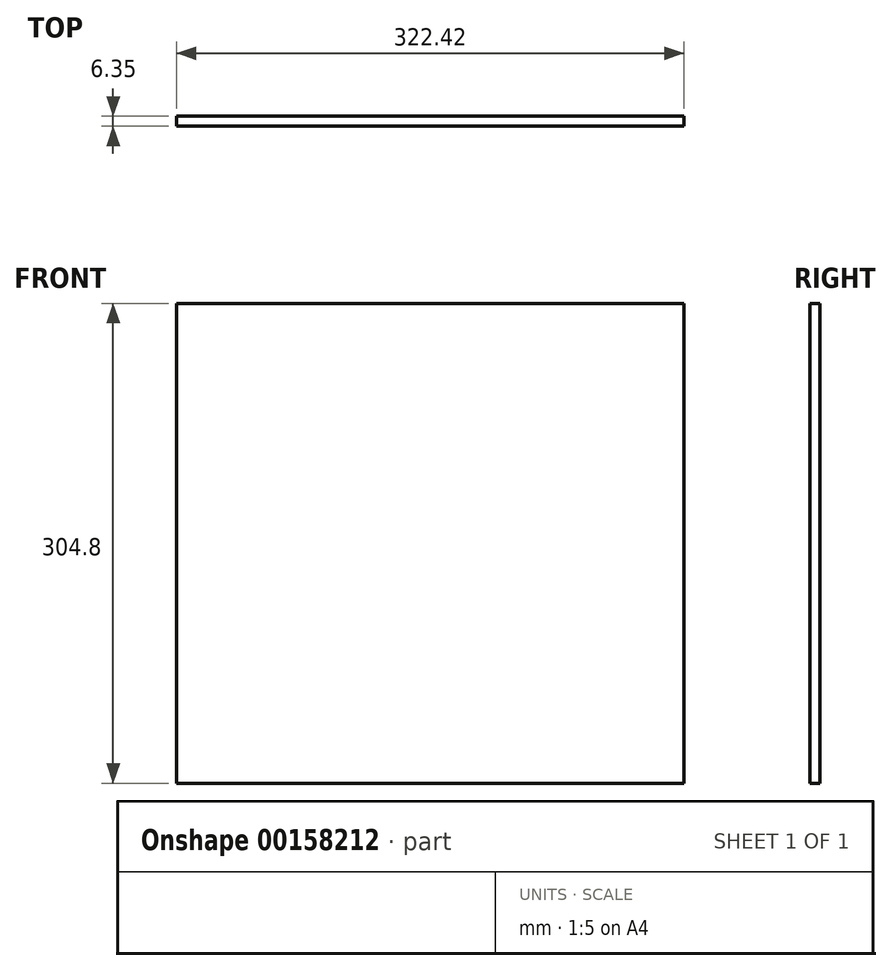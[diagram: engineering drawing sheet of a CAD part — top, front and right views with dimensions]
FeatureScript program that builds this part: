
annotation { "Feature Type Name" : "Feature", "Feature Type Description" : "" }
export const myFeature = defineFeature(function(context is Context, id is Id, definition is map)
    precondition{}
    {
        {
            var Q0;
            Q0=qCreatedBy(makeId("Front.planeOp"),FACE);
            var sketch = newSketch(context, id + "F0", { "sketchPlane" : qUnion([Q0])});
            skLineSegment(sketch, "E0.bottom", {"start": v(161.2, 152.4) * mm, "end": v(-161.2, 152.4) * mm});
            skLineSegment(sketch, "E0.top", {"start": v(161.2, -152.4) * mm, "end": v(-161.2, -152.4) * mm});
            skLineSegment(sketch, "E0.left", {"start": v(161.2, 152.4) * mm, "end": v(161.2, -152.4) * mm});
            skLineSegment(sketch, "E0.right", {"start": v(-161.2, 152.4) * mm, "end": v(-161.2, -152.4) * mm});
            skPoint(sketch, "E0.middle", {"position": v(0, 0) * mm});
            skSolve(sketch);
        }
        {
            var Q0;
            Q0=makeQuery(id+"F0.imprint","IMPRINT",FACE,{"disambiguationData":[TD([[makeQuery(id+"F0.imprint","IMPRINT",EDGE,{"derivedFrom":sQuery(id+"F0.wireOp",EDGE,"E0.bottom")}),1.0]])]});
            extrude(context, id + "F1", {"entities" : qUnion([Q0]), "depth" : 6.35 * mm});
        }
    });
